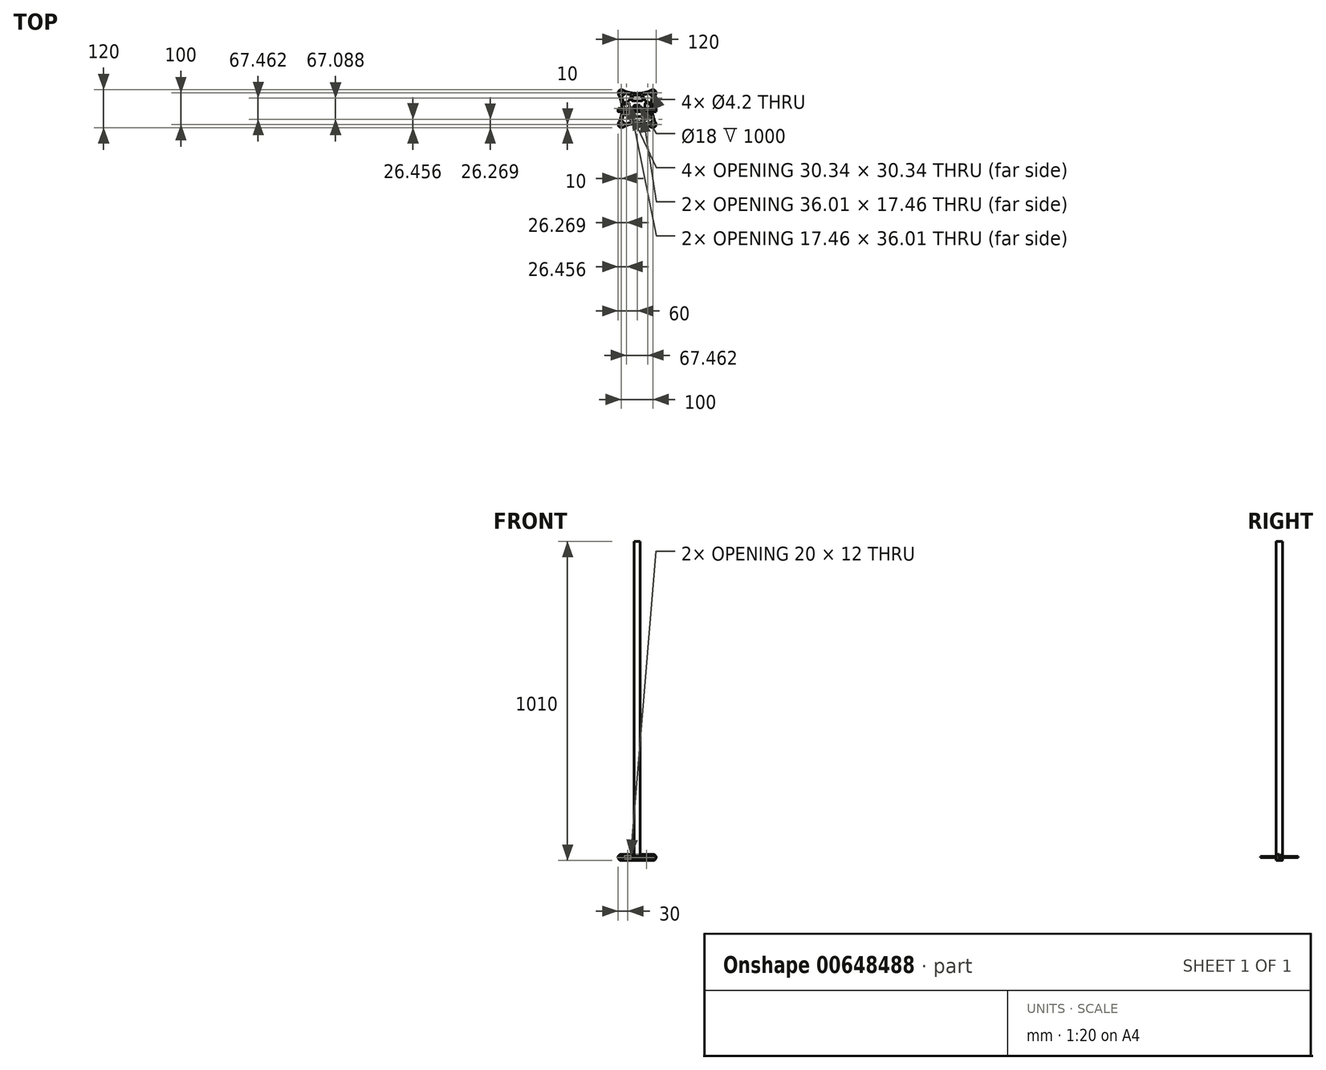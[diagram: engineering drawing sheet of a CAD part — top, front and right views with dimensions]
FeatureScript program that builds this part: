
annotation { "Feature Type Name" : "Feature", "Feature Type Description" : "" }
export const myFeature = defineFeature(function(context is Context, id is Id, definition is map)
    precondition{}
    {
        {
            var Q0;
            Q0=qCreatedBy(makeId("Top.planeOp"),FACE);
            var sketch = newSketch(context, id + "F0", { "sketchPlane" : qUnion([Q0])});
            skCircle(sketch, "E0", {"center": v(0, 0) * mm, "radius": 10 * mm});
            skCircle(sketch, "E1", {"center": v(0, 0) * mm, "radius": 9 * mm});
            skSolve(sketch);
        }
        {
            var Q0;
            Q0=makeQuery(id+"F0.imprint","IMPRINT",FACE,{"disambiguationData":[TD([[makeQuery(id+"F0.imprint","IMPRINT",EDGE,{"derivedFrom":sQuery(id+"F0.wireOp",EDGE,"335d696f-6c34-485e-b587-ec5af4deedc00.MirrorC")}),1.0]])]});
            var Q1;
            Q1=makeQuery(id+"F0.imprint","IMPRINT",FACE,{"disambiguationData":[TD([[makeQuery(id+"F0.imprint","IMPRINT",EDGE,{"derivedFrom":sQuery(id+"F0.wireOp",EDGE,"E0")}),1.0]])]});
            extrude(context, id + "F1", {"entities" : qUnion([Q0, Q1]), "depth" : 1000 * mm, "offsetDistance" : 25 * mm});
        }
        {
            var Q0;
            Q0=qCreatedBy(makeId("Top.planeOp"),FACE);
            var sketch = newSketch(context, id + "F2", { "sketchPlane" : qUnion([Q0])});
            skLineSegment(sketch, "E2", {"start": v(0, 0) * mm, "end": v(9, 0) * mm});
            skLineSegment(sketch, "E3", {"start": v(9, 0) * mm, "end": v(9, 7) * mm});
            skLineSegment(sketch, "E4", {"start": v(9, 7) * mm, "end": v(10, 7) * mm});
            skLineSegment(sketch, "E5", {"start": v(10, 7) * mm, "end": v(10, 10) * mm});
            skLineSegment(sketch, "E6", {"start": v(10, 10) * mm, "end": v(2.5, 10) * mm});
            skLineSegment(sketch, "E7", {"start": v(2.5, 10) * mm, "end": v(2.5, 4) * mm});
            skLineSegment(sketch, "E8", {"start": v(2.5, 4) * mm, "end": v(0, 4) * mm});
            skLineSegment(sketch, "E9", {"start": v(0, 4) * mm, "end": v(0, 0) * mm});
            skLineSegment(sketch, "E10", {"start": v(0, 20) * mm, "end": v(0, -14.34) * mm, "construction": true});
            skSolve(sketch);
        }
        {
            var Q0;
            Q0=makeQuery(id+"F2.imprint","IMPRINT",FACE,{"disambiguationData":[TD([[makeQuery(id+"F2.imprint","IMPRINT",EDGE,{"derivedFrom":sQuery(id+"F2.wireOp",EDGE,"E2")}),1.0]])]});
            var Q1;
            Q1=sQuery(id+"F2.wireOp",EDGE,"E10");
            revolve(context, id + "F3", {"surfaceOperationType" : NewSurfaceOperationType.NEW, "entities" : qUnion([Q0]), "axis" : qUnion([Q1]), "revolveType" : RevolveType.FULL});
        }
        {
            var Q0;
            Q0=qCreatedBy(makeId("Front.planeOp"),FACE);
            var sketch = newSketch(context, id + "F4", { "sketchPlane" : qUnion([Q0])});
            skCircle(sketch, "E11", {"center": v(50, 0) * mm, "radius": 3.1 * mm});
            skArc(sketch, "E12", {"start": v(50, -10) * mm, "mid": v(60, 0) * mm, "end": v(50, 10) * mm});
            skLineSegment(sketch, "E13.bottom", {"start": v(40, 6) * mm, "end": v(20, 6) * mm});
            skLineSegment(sketch, "E13.top", {"start": v(40, -6) * mm, "end": v(20, -6) * mm});
            skLineSegment(sketch, "E13.left", {"start": v(40, 6) * mm, "end": v(40, -6) * mm});
            skLineSegment(sketch, "E13.right", {"start": v(20, 6) * mm, "end": v(20, -6) * mm});
            skPoint(sketch, "E13.middle", {"position": v(30, 0) * mm});
            skLineSegment(sketch, "E14.MirrorCS", {"start": v(-20, 6) * mm, "end": v(-20, -6) * mm});
            skLineSegment(sketch, "E15.MirrorCS", {"start": v(-40, 6) * mm, "end": v(-20, 6) * mm});
            skLineSegment(sketch, "E16.MirrorCS", {"start": v(-40, -6) * mm, "end": v(-20, -6) * mm});
            skLineSegment(sketch, "E17.MirrorCS", {"start": v(-40, 6) * mm, "end": v(-40, -6) * mm});
            skArc(sketch, "E18.MirrorCS", {"start": v(-50, -10) * mm, "mid": v(-60, 0) * mm, "end": v(-50, 10) * mm});
            skCircle(sketch, "E19.MirrorC", {"center": v(-50, 0) * mm, "radius": 3.1 * mm});
            skLineSegment(sketch, "E20", {"start": v(50, 10) * mm, "end": v(15, 10) * mm});
            skLineSegment(sketch, "E21", {"start": v(15, 10) * mm, "end": v(15, 6.3) * mm});
            skLineSegment(sketch, "E22", {"start": v(15, 6.3) * mm, "end": v(5.1, 6.3) * mm});
            skLineSegment(sketch, "E23", {"start": v(5.1, 6.3) * mm, "end": v(5.1, -6) * mm});
            skLineSegment(sketch, "E24", {"start": v(5.1, -6) * mm, "end": v(0, -6) * mm});
            skLineSegment(sketch, "E25.MirrorCS", {"start": v(-5.1, -6) * mm, "end": v(0, -6) * mm});
            skLineSegment(sketch, "E26.MirrorCS", {"start": v(-5.1, 6.3) * mm, "end": v(-5.1, -6) * mm});
            skLineSegment(sketch, "E27.MirrorCS", {"start": v(-15, 6.3) * mm, "end": v(-5.1, 6.3) * mm});
            skLineSegment(sketch, "E28.MirrorCS", {"start": v(-15, 10) * mm, "end": v(-15, 6.3) * mm});
            skLineSegment(sketch, "E29.MirrorCS", {"start": v(-50, 10) * mm, "end": v(-15, 10) * mm});
            skLineSegment(sketch, "E30", {"start": v(50, -10) * mm, "end": v(0, -10) * mm});
            skLineSegment(sketch, "E31.MirrorCS", {"start": v(-50, -10) * mm, "end": v(0, -10) * mm});
            skSolve(sketch);
        }
        {
            var Q0;
            Q0=makeQuery(id+"F4.imprint","IMPRINT",FACE,{"disambiguationData":[TD([[makeQuery(id+"F4.imprint","IMPRINT",EDGE,{"derivedFrom":sQuery(id+"F4.wireOp",EDGE,"E11")}),-1.0]])]});
            extrude(context, id + "F5", {"entities" : qUnion([Q0]), "depth" : 10 * mm, "offsetDistance" : 25 * mm});
        }
        {
            var Q0;
            Q0=makeQuery(id+"F5.opExtrude","SWEPT_EDGE",EDGE,{"disambiguationData":[OSD([sQuery(id+"F4.wireOp",EDGE,"E15.MirrorCS"),sQuery(id+"F4.wireOp",EDGE,"E17.MirrorCS")])]});
            var Q1;
            Q1=makeQuery(id+"F5.opExtrude","SWEPT_EDGE",EDGE,{"disambiguationData":[OSD([sQuery(id+"F4.wireOp",EDGE,"E14.MirrorCS"),sQuery(id+"F4.wireOp",EDGE,"E15.MirrorCS")])]});
            var Q2;
            Q2=makeQuery(id+"F5.opExtrude","SWEPT_EDGE",EDGE,{"disambiguationData":[OSD([sQuery(id+"F4.wireOp",EDGE,"E14.MirrorCS"),sQuery(id+"F4.wireOp",EDGE,"E16.MirrorCS")])]});
            var Q3;
            Q3=makeQuery(id+"F5.opExtrude","SWEPT_EDGE",EDGE,{"disambiguationData":[OSD([sQuery(id+"F4.wireOp",EDGE,"E13.top"),sQuery(id+"F4.wireOp",EDGE,"E13.left")])]});
            var Q4;
            Q4=makeQuery(id+"F5.opExtrude","SWEPT_EDGE",EDGE,{"disambiguationData":[OSD([sQuery(id+"F4.wireOp",EDGE,"E16.MirrorCS"),sQuery(id+"F4.wireOp",EDGE,"E17.MirrorCS")])]});
            var Q5;
            Q5=makeQuery(id+"F5.opExtrude","SWEPT_EDGE",EDGE,{"disambiguationData":[OSD([sQuery(id+"F4.wireOp",EDGE,"E13.top"),sQuery(id+"F4.wireOp",EDGE,"E13.right")])]});
            var Q6;
            Q6=makeQuery(id+"F5.opExtrude","SWEPT_EDGE",EDGE,{"disambiguationData":[OSD([sQuery(id+"F4.wireOp",EDGE,"E13.bottom"),sQuery(id+"F4.wireOp",EDGE,"E13.left")])]});
            var Q7;
            Q7=makeQuery(id+"F5.opExtrude","SWEPT_EDGE",EDGE,{"disambiguationData":[OSD([sQuery(id+"F4.wireOp",EDGE,"E13.bottom"),sQuery(id+"F4.wireOp",EDGE,"E13.right")])]});
            var Q8;
            Q8=makeQuery(id+"F5.opExtrude","SWEPT_EDGE",EDGE,{"disambiguationData":[OSD([sQuery(id+"F4.wireOp",EDGE,"E25.MirrorCS"),sQuery(id+"F4.wireOp",EDGE,"E26.MirrorCS")])]});
            var Q9;
            Q9=makeQuery(id+"F5.opExtrude","SWEPT_EDGE",EDGE,{"disambiguationData":[OSD([sQuery(id+"F4.wireOp",EDGE,"E23"),sQuery(id+"F4.wireOp",EDGE,"E24")])]});
            fillet(context, id + "F6", {"entities" : qUnion([Q0, Q1, Q2, Q3, Q4, Q5, Q6, Q7, Q8, Q9]), "radius" : 3 * mm, "tangentPropagation" : true, "allowEdgeOverflow" : false});
        }
        {
            var Q0;
            Q0=qCreatedBy(makeId("Top.planeOp"),FACE);
            var sketch = newSketch(context, id + "F7", { "sketchPlane" : qUnion([Q0])});
            skLineSegment(sketch, "E32.bottom", {"start": v(50, 50) * mm, "end": v(-50, 50) * mm, "construction": true});
            skLineSegment(sketch, "E32.top", {"start": v(50, -50) * mm, "end": v(-50, -50) * mm, "construction": true});
            skLineSegment(sketch, "E32.left", {"start": v(50, 50) * mm, "end": v(50, -50) * mm, "construction": true});
            skLineSegment(sketch, "E32.right", {"start": v(-50, 50) * mm, "end": v(-50, -50) * mm, "construction": true});
            skPoint(sketch, "E32.middle", {"position": v(0, 0) * mm});
            skArc(sketch, "E33", {"start": v(0, 48) * mm, "mid": v(23.12, 50.7) * mm, "end": v(45, 58.66) * mm});
            skArc(sketch, "E34", {"start": v(45, 58.66) * mm, "mid": v(57.07, 57.07) * mm, "end": v(58.66, 45) * mm});
            skArc(sketch, "E35", {"start": v(58.66, 45) * mm, "mid": v(50.7, 23.12) * mm, "end": v(48, 0) * mm});
            skLineSegment(sketch, "E36", {"start": v(50, 50) * mm, "end": v(45, 58.66) * mm, "construction": true});
            skLineSegment(sketch, "E37", {"start": v(50, 50) * mm, "end": v(58.66, 45) * mm, "construction": true});
            skCircle(sketch, "E38", {"center": v(50, 50) * mm, "radius": 2.1 * mm});
            skArc(sketch, "E39.MirrorCS", {"start": v(0, 48) * mm, "mid": v(-23.12, 50.7) * mm, "end": v(-45, 58.66) * mm});
            skArc(sketch, "E40.MirrorCS", {"start": v(-45, 58.66) * mm, "mid": v(-57.07, 57.07) * mm, "end": v(-58.66, 45) * mm});
            skCircle(sketch, "E41.MirrorC", {"center": v(-50, 50) * mm, "radius": 2.1 * mm});
            skArc(sketch, "E42.MirrorCS", {"start": v(-58.66, 45) * mm, "mid": v(-50.7, 23.12) * mm, "end": v(-48, 0) * mm});
            skArc(sketch, "E43.MirrorCS", {"start": v(-58.66, -45) * mm, "mid": v(-50.7, -23.12) * mm, "end": v(-48, 0) * mm});
            skArc(sketch, "E44.MirrorCS", {"start": v(-45, -58.66) * mm, "mid": v(-57.07, -57.07) * mm, "end": v(-58.66, -45) * mm});
            skCircle(sketch, "E45.MirrorC", {"center": v(-50, -50) * mm, "radius": 2.1 * mm});
            skArc(sketch, "E46.MirrorCS", {"start": v(0, -48) * mm, "mid": v(-23.12, -50.7) * mm, "end": v(-45, -58.66) * mm});
            skArc(sketch, "E47.MirrorCS", {"start": v(0, -48) * mm, "mid": v(23.12, -50.7) * mm, "end": v(45, -58.66) * mm});
            skArc(sketch, "E48.MirrorCS", {"start": v(45, -58.66) * mm, "mid": v(57.07, -57.07) * mm, "end": v(58.66, -45) * mm});
            skArc(sketch, "E49.MirrorCS", {"start": v(58.66, -45) * mm, "mid": v(50.7, -23.12) * mm, "end": v(48, 0) * mm});
            skCircle(sketch, "E50.MirrorC", {"center": v(50, -50) * mm, "radius": 2.1 * mm});
            skArc(sketch, "E51", {"start": v(40, 49.81) * mm, "mid": v(42.93, 42.93) * mm, "end": v(49.81, 40) * mm});
            skArc(sketch, "E52", {"start": v(0, 42) * mm, "mid": v(6, 42.17) * mm, "end": v(12, 42.68) * mm});
            skArc(sketch, "E53", {"start": v(40, 49.81) * mm, "mid": v(28.75, 45.96) * mm, "end": v(17.13, 43.39) * mm});
            skLineSegment(sketch, "E54", {"start": v(0, 25) * mm, "end": v(19.56, 25) * mm});
            skLineSegment(sketch, "E55", {"start": v(19.56, 25) * mm, "end": v(12, 42.68) * mm});
            skLineSegment(sketch, "E56", {"start": v(25, 25) * mm, "end": v(17.13, 43.39) * mm});
            skArc(sketch, "E57", {"start": v(49.81, 40) * mm, "mid": v(45.96, 28.75) * mm, "end": v(43.39, 17.13) * mm});
            skArc(sketch, "E58", {"start": v(42.68, 12) * mm, "mid": v(42.17, 6) * mm, "end": v(42, 0) * mm});
            skLineSegment(sketch, "E59", {"start": v(25, 25) * mm, "end": v(43.39, 17.13) * mm});
            skLineSegment(sketch, "E60", {"start": v(42.68, 12) * mm, "end": v(25, 19.56) * mm});
            skLineSegment(sketch, "E61", {"start": v(25, 19.56) * mm, "end": v(25, 0) * mm});
            skLineSegment(sketch, "E62.MirrorCS", {"start": v(0, 25) * mm, "end": v(-19.56, 25) * mm});
            skArc(sketch, "E63.MirrorCS", {"start": v(0, 42) * mm, "mid": v(-6, 42.17) * mm, "end": v(-12, 42.68) * mm});
            skArc(sketch, "E64.MirrorCS", {"start": v(-40, 49.81) * mm, "mid": v(-28.75, 45.96) * mm, "end": v(-17.13, 43.39) * mm});
            skArc(sketch, "E65.MirrorCS", {"start": v(-40, 49.81) * mm, "mid": v(-42.93, 42.93) * mm, "end": v(-49.81, 40) * mm});
            skArc(sketch, "E66.MirrorCS", {"start": v(-49.81, 40) * mm, "mid": v(-45.96, 28.75) * mm, "end": v(-43.39, 17.13) * mm});
            skLineSegment(sketch, "E67.MirrorCS", {"start": v(-25, 25) * mm, "end": v(-43.39, 17.13) * mm});
            skLineSegment(sketch, "E68.MirrorCS", {"start": v(-19.56, 25) * mm, "end": v(-12, 42.68) * mm});
            skLineSegment(sketch, "E69.MirrorCS", {"start": v(-25, 25) * mm, "end": v(-17.13, 43.39) * mm});
            skLineSegment(sketch, "E70.MirrorCS", {"start": v(-42.68, 12) * mm, "end": v(-25, 19.56) * mm});
            skLineSegment(sketch, "E71.MirrorCS", {"start": v(-25, 19.56) * mm, "end": v(-25, 0) * mm});
            skArc(sketch, "E72.MirrorCS", {"start": v(-42.68, 12) * mm, "mid": v(-42.17, 6) * mm, "end": v(-42, 0) * mm});
            skArc(sketch, "E73.MirrorCS", {"start": v(-42.68, -12) * mm, "mid": v(-42.17, -6) * mm, "end": v(-42, 0) * mm});
            skLineSegment(sketch, "E74.MirrorCS", {"start": v(-42.68, -12) * mm, "end": v(-25, -19.56) * mm});
            skLineSegment(sketch, "E75.MirrorCS", {"start": v(-25, -19.56) * mm, "end": v(-25, 0) * mm});
            skLineSegment(sketch, "E76.MirrorCS", {"start": v(-25, -25) * mm, "end": v(-17.13, -43.39) * mm});
            skLineSegment(sketch, "E77.MirrorCS", {"start": v(-25, -25) * mm, "end": v(-43.39, -17.13) * mm});
            skArc(sketch, "E78.MirrorCS", {"start": v(-49.81, -40) * mm, "mid": v(-45.96, -28.75) * mm, "end": v(-43.39, -17.13) * mm});
            skArc(sketch, "E79.MirrorCS", {"start": v(-40, -49.81) * mm, "mid": v(-42.93, -42.93) * mm, "end": v(-49.81, -40) * mm});
            skArc(sketch, "E80.MirrorCS", {"start": v(-40, -49.81) * mm, "mid": v(-28.75, -45.96) * mm, "end": v(-17.13, -43.39) * mm});
            skArc(sketch, "E81.MirrorCS", {"start": v(0, -42) * mm, "mid": v(-6, -42.17) * mm, "end": v(-12, -42.68) * mm});
            skLineSegment(sketch, "E82.MirrorCS", {"start": v(0, -25) * mm, "end": v(-19.56, -25) * mm});
            skLineSegment(sketch, "E83.MirrorCS", {"start": v(0, -25) * mm, "end": v(19.56, -25) * mm});
            skLineSegment(sketch, "E84.MirrorCS", {"start": v(19.56, -25) * mm, "end": v(12, -42.68) * mm});
            skLineSegment(sketch, "E85.MirrorCS", {"start": v(-19.56, -25) * mm, "end": v(-12, -42.68) * mm});
            skArc(sketch, "E86.MirrorCS", {"start": v(0, -42) * mm, "mid": v(6, -42.17) * mm, "end": v(12, -42.68) * mm});
            skArc(sketch, "E87.MirrorCS", {"start": v(40, -49.81) * mm, "mid": v(28.75, -45.96) * mm, "end": v(17.13, -43.39) * mm});
            skLineSegment(sketch, "E88.MirrorCS", {"start": v(25, -25) * mm, "end": v(17.13, -43.39) * mm});
            skLineSegment(sketch, "E89.MirrorCS", {"start": v(25, -25) * mm, "end": v(43.39, -17.13) * mm});
            skArc(sketch, "E90.MirrorCS", {"start": v(49.81, -40) * mm, "mid": v(45.96, -28.75) * mm, "end": v(43.39, -17.13) * mm});
            skArc(sketch, "E91.MirrorCS", {"start": v(40, -49.81) * mm, "mid": v(42.93, -42.93) * mm, "end": v(49.81, -40) * mm});
            skLineSegment(sketch, "E92.MirrorCS", {"start": v(25, -19.56) * mm, "end": v(25, 0) * mm});
            skLineSegment(sketch, "E93.MirrorCS", {"start": v(42.68, -12) * mm, "end": v(25, -19.56) * mm});
            skArc(sketch, "E94.MirrorCS", {"start": v(42.68, -12) * mm, "mid": v(42.17, -6) * mm, "end": v(42, 0) * mm});
            skSolve(sketch);
        }
        {
            var Q0;
            Q0=makeQuery(id+"F7.imprint","IMPRINT",FACE,{"disambiguationData":[TD([[makeQuery(id+"F7.imprint","IMPRINT",EDGE,{"derivedFrom":sQuery(id+"F7.wireOp",EDGE,"E33")}),-1.0]])]});
            extrude(context, id + "F8", {"entities" : qUnion([Q0]), "depth" : 3.7 * mm, "offsetDistance" : 25 * mm});
        }
        {
            var Q0;
            Q0=makeQuery(id+"F8.opExtrude","SWEPT_EDGE",EDGE,{"disambiguationData":[OSD([sQuery(id+"F7.wireOp",EDGE,"E64.MirrorCS"),sQuery(id+"F7.wireOp",EDGE,"E65.MirrorCS")])]});
            var Q1;
            Q1=makeQuery(id+"F8.opExtrude","SWEPT_EDGE",EDGE,{"disambiguationData":[OSD([sQuery(id+"F7.wireOp",EDGE,"E65.MirrorCS"),sQuery(id+"F7.wireOp",EDGE,"E66.MirrorCS")])]});
            var Q2;
            Q2=makeQuery(id+"F8.opExtrude","SWEPT_EDGE",EDGE,{"disambiguationData":[OSD([sQuery(id+"F7.wireOp",EDGE,"E64.MirrorCS"),sQuery(id+"F7.wireOp",EDGE,"E69.MirrorCS")])]});
            var Q3;
            Q3=makeQuery(id+"F8.opExtrude","SWEPT_EDGE",EDGE,{"disambiguationData":[OSD([sQuery(id+"F7.wireOp",EDGE,"E67.MirrorCS"),sQuery(id+"F7.wireOp",EDGE,"E69.MirrorCS")])]});
            var Q4;
            Q4=makeQuery(id+"F8.opExtrude","SWEPT_EDGE",EDGE,{"disambiguationData":[OSD([sQuery(id+"F7.wireOp",EDGE,"E66.MirrorCS"),sQuery(id+"F7.wireOp",EDGE,"E67.MirrorCS")])]});
            var Q5;
            Q5=makeQuery(id+"F8.opExtrude","SWEPT_EDGE",EDGE,{"disambiguationData":[OSD([sQuery(id+"F7.wireOp",EDGE,"E73.MirrorCS"),sQuery(id+"F7.wireOp",EDGE,"E74.MirrorCS")])]});
            var Q6;
            Q6=makeQuery(id+"F8.opExtrude","SWEPT_EDGE",EDGE,{"disambiguationData":[OSD([sQuery(id+"F7.wireOp",EDGE,"E78.MirrorCS"),sQuery(id+"F7.wireOp",EDGE,"E79.MirrorCS")])]});
            var Q7;
            Q7=makeQuery(id+"F8.opExtrude","SWEPT_EDGE",EDGE,{"disambiguationData":[OSD([sQuery(id+"F7.wireOp",EDGE,"E79.MirrorCS"),sQuery(id+"F7.wireOp",EDGE,"E80.MirrorCS")])]});
            var Q8;
            Q8=makeQuery(id+"F8.opExtrude","SWEPT_EDGE",EDGE,{"disambiguationData":[OSD([sQuery(id+"F7.wireOp",EDGE,"E70.MirrorCS"),sQuery(id+"F7.wireOp",EDGE,"E72.MirrorCS")])]});
            var Q9;
            Q9=makeQuery(id+"F8.opExtrude","SWEPT_EDGE",EDGE,{"disambiguationData":[OSD([sQuery(id+"F7.wireOp",EDGE,"E76.MirrorCS"),sQuery(id+"F7.wireOp",EDGE,"E77.MirrorCS")])]});
            var Q10;
            Q10=makeQuery(id+"F8.opExtrude","SWEPT_EDGE",EDGE,{"disambiguationData":[OSD([sQuery(id+"F7.wireOp",EDGE,"E63.MirrorCS"),sQuery(id+"F7.wireOp",EDGE,"E68.MirrorCS")])]});
            var Q11;
            Q11=makeQuery(id+"F8.opExtrude","SWEPT_EDGE",EDGE,{"disambiguationData":[OSD([sQuery(id+"F7.wireOp",EDGE,"E52"),sQuery(id+"F7.wireOp",EDGE,"E55")])]});
            var Q12;
            Q12=makeQuery(id+"F8.opExtrude","SWEPT_EDGE",EDGE,{"disambiguationData":[OSD([sQuery(id+"F7.wireOp",EDGE,"E70.MirrorCS"),sQuery(id+"F7.wireOp",EDGE,"E71.MirrorCS")])]});
            var Q13;
            Q13=makeQuery(id+"F8.opExtrude","SWEPT_EDGE",EDGE,{"disambiguationData":[OSD([sQuery(id+"F7.wireOp",EDGE,"E54"),sQuery(id+"F7.wireOp",EDGE,"E55")])]});
            var Q14;
            Q14=makeQuery(id+"F8.opExtrude","SWEPT_EDGE",EDGE,{"disambiguationData":[OSD([sQuery(id+"F7.wireOp",EDGE,"E57"),sQuery(id+"F7.wireOp",EDGE,"E59")])]});
            var Q15;
            Q15=makeQuery(id+"F8.opExtrude","SWEPT_EDGE",EDGE,{"disambiguationData":[OSD([sQuery(id+"F7.wireOp",EDGE,"E93.MirrorCS"),sQuery(id+"F7.wireOp",EDGE,"E94.MirrorCS")])]});
            var Q16;
            Q16=makeQuery(id+"F8.opExtrude","SWEPT_EDGE",EDGE,{"disambiguationData":[OSD([sQuery(id+"F7.wireOp",EDGE,"E90.MirrorCS"),sQuery(id+"F7.wireOp",EDGE,"E91.MirrorCS")])]});
            var Q17;
            Q17=makeQuery(id+"F8.opExtrude","SWEPT_EDGE",EDGE,{"disambiguationData":[OSD([sQuery(id+"F7.wireOp",EDGE,"E84.MirrorCS"),sQuery(id+"F7.wireOp",EDGE,"E86.MirrorCS")])]});
            var Q18;
            Q18=makeQuery(id+"F8.opExtrude","SWEPT_EDGE",EDGE,{"disambiguationData":[OSD([sQuery(id+"F7.wireOp",EDGE,"E76.MirrorCS"),sQuery(id+"F7.wireOp",EDGE,"E80.MirrorCS")])]});
            var Q19;
            Q19=makeQuery(id+"F8.opExtrude","SWEPT_EDGE",EDGE,{"disambiguationData":[OSD([sQuery(id+"F7.wireOp",EDGE,"E74.MirrorCS"),sQuery(id+"F7.wireOp",EDGE,"E75.MirrorCS")])]});
            var Q20;
            Q20=makeQuery(id+"F8.opExtrude","SWEPT_EDGE",EDGE,{"disambiguationData":[OSD([sQuery(id+"F7.wireOp",EDGE,"E87.MirrorCS"),sQuery(id+"F7.wireOp",EDGE,"E91.MirrorCS")])]});
            var Q21;
            Q21=makeQuery(id+"F8.opExtrude","SWEPT_EDGE",EDGE,{"disambiguationData":[OSD([sQuery(id+"F7.wireOp",EDGE,"E58"),sQuery(id+"F7.wireOp",EDGE,"E60")])]});
            var Q22;
            Q22=makeQuery(id+"F8.opExtrude","SWEPT_EDGE",EDGE,{"disambiguationData":[OSD([sQuery(id+"F7.wireOp",EDGE,"E83.MirrorCS"),sQuery(id+"F7.wireOp",EDGE,"E84.MirrorCS")])]});
            var Q23;
            Q23=makeQuery(id+"F8.opExtrude","SWEPT_EDGE",EDGE,{"disambiguationData":[OSD([sQuery(id+"F7.wireOp",EDGE,"E89.MirrorCS"),sQuery(id+"F7.wireOp",EDGE,"E90.MirrorCS")])]});
            var Q24;
            Q24=makeQuery(id+"F8.opExtrude","SWEPT_EDGE",EDGE,{"disambiguationData":[OSD([sQuery(id+"F7.wireOp",EDGE,"E51"),sQuery(id+"F7.wireOp",EDGE,"E57")])]});
            var Q25;
            Q25=makeQuery(id+"F8.opExtrude","SWEPT_EDGE",EDGE,{"disambiguationData":[OSD([sQuery(id+"F7.wireOp",EDGE,"E51"),sQuery(id+"F7.wireOp",EDGE,"E53")])]});
            var Q26;
            Q26=makeQuery(id+"F8.opExtrude","SWEPT_EDGE",EDGE,{"disambiguationData":[OSD([sQuery(id+"F7.wireOp",EDGE,"E60"),sQuery(id+"F7.wireOp",EDGE,"E61")])]});
            var Q27;
            Q27=makeQuery(id+"F8.opExtrude","SWEPT_EDGE",EDGE,{"disambiguationData":[OSD([sQuery(id+"F7.wireOp",EDGE,"E53"),sQuery(id+"F7.wireOp",EDGE,"E56")])]});
            var Q28;
            Q28=makeQuery(id+"F8.opExtrude","SWEPT_EDGE",EDGE,{"disambiguationData":[OSD([sQuery(id+"F7.wireOp",EDGE,"E82.MirrorCS"),sQuery(id+"F7.wireOp",EDGE,"E85.MirrorCS")])]});
            var Q29;
            Q29=makeQuery(id+"F8.opExtrude","SWEPT_EDGE",EDGE,{"disambiguationData":[OSD([sQuery(id+"F7.wireOp",EDGE,"E88.MirrorCS"),sQuery(id+"F7.wireOp",EDGE,"E89.MirrorCS")])]});
            var Q30;
            Q30=makeQuery(id+"F8.opExtrude","SWEPT_EDGE",EDGE,{"disambiguationData":[OSD([sQuery(id+"F7.wireOp",EDGE,"E81.MirrorCS"),sQuery(id+"F7.wireOp",EDGE,"E85.MirrorCS")])]});
            var Q31;
            Q31=makeQuery(id+"F8.opExtrude","SWEPT_EDGE",EDGE,{"disambiguationData":[OSD([sQuery(id+"F7.wireOp",EDGE,"E87.MirrorCS"),sQuery(id+"F7.wireOp",EDGE,"E88.MirrorCS")])]});
            var Q32;
            Q32=makeQuery(id+"F8.opExtrude","SWEPT_EDGE",EDGE,{"disambiguationData":[OSD([sQuery(id+"F7.wireOp",EDGE,"E56"),sQuery(id+"F7.wireOp",EDGE,"E59")])]});
            var Q33;
            Q33=makeQuery(id+"F8.opExtrude","SWEPT_EDGE",EDGE,{"disambiguationData":[OSD([sQuery(id+"F7.wireOp",EDGE,"E62.MirrorCS"),sQuery(id+"F7.wireOp",EDGE,"E68.MirrorCS")])]});
            var Q34;
            Q34=makeQuery(id+"F8.opExtrude","SWEPT_EDGE",EDGE,{"disambiguationData":[OSD([sQuery(id+"F7.wireOp",EDGE,"E92.MirrorCS"),sQuery(id+"F7.wireOp",EDGE,"E93.MirrorCS")])]});
            var Q35;
            Q35=makeQuery(id+"F8.opExtrude","SWEPT_EDGE",EDGE,{"disambiguationData":[OSD([sQuery(id+"F7.wireOp",EDGE,"E77.MirrorCS"),sQuery(id+"F7.wireOp",EDGE,"E78.MirrorCS")])]});
            fillet(context, id + "F9", {"entities" : qUnion([Q0, Q1, Q2, Q3, Q4, Q5, Q6, Q7, Q8, Q9, Q10, Q11, Q12, Q13, Q14, Q15, Q16, Q17, Q18, Q19, Q20, Q21, Q22, Q23, Q24, Q25, Q26, Q27, Q28, Q29, Q30, Q31, Q32, Q33, Q34, Q35]), "radius" : 3 * mm, "tangentPropagation" : true, "allowEdgeOverflow" : false});
        }
        {
            var Q0;
            Q0=qCreatedBy(makeId("Top.planeOp"),FACE);
            var sketch = newSketch(context, id + "F10", { "sketchPlane" : qUnion([Q0])});
            skLineSegment(sketch, "E95.bottom", {"start": v(14.9, 5) * mm, "end": v(-14.9, 5) * mm});
            skLineSegment(sketch, "E95.top", {"start": v(14.9, -5) * mm, "end": v(-14.9, -5) * mm});
            skLineSegment(sketch, "E95.left", {"start": v(14.9, 5) * mm, "end": v(14.9, -5) * mm});
            skLineSegment(sketch, "E95.right", {"start": v(-14.9, 5) * mm, "end": v(-14.9, -5) * mm});
            skPoint(sketch, "E95.middle", {"position": v(0, 0) * mm});
            skCircle(sketch, "E96", {"center": v(10, 0) * mm, "radius": 1.6 * mm});
            skCircle(sketch, "E97.MirrorC", {"center": v(-10, 0) * mm, "radius": 1.6 * mm});
            skSolve(sketch);
        }
        {
            var Q0;
            Q0=makeQuery(id+"F10.imprint","IMPRINT",FACE,{"disambiguationData":[TD([[makeQuery(id+"F10.imprint","IMPRINT",EDGE,{"derivedFrom":sQuery(id+"F10.wireOp",EDGE,"E95.bottom")}),1.0]])]});
            extrude(context, id + "F11", {"entities" : qUnion([Q0]), "depth" : 3.7 * mm, "offsetDistance" : 25 * mm});
        }
        {
            var Q0;
            Q0=makeQuery(id+"F5.opExtrude","SWEPT_FACE",FACE,{"disambiguationData":[OSD([sQuery(id+"F4.wireOp",EDGE,"E27.MirrorCS")])]});
            var sketch = newSketch(context, id + "F12", { "sketchPlane" : qUnion([Q0])});
            skPoint(sketch, "E98", {"position": v(-10.05, -5) * mm});
            skPoint(sketch, "E98.positionSnap0", {"position": v(-10.05, 0) * mm});
            skPoint(sketch, "E98.positionSnap1", {"position": v(-5.1, -5) * mm});
            skPoint(sketch, "E99", {"position": v(10.1, -5) * mm});
            skSolve(sketch);
        }
        {
            var Q0;
            Q0=sQuery(id+"F12.wireOp",VERTEX,"E98");
            var Q1;
            Q1=sQuery(id+"F12.wireOp",VERTEX,"E99");
            var Q2;
            Q2=makeQuery(id+"F5.opExtrude","SWEPT_BODY",BODY,{"disambiguationData":[OSD([sQuery(id+"F4.wireOp",EDGE,"E11"),sQuery(id+"F4.wireOp",EDGE,"E12"),sQuery(id+"F4.wireOp",EDGE,"E13.bottom"),sQuery(id+"F4.wireOp",EDGE,"E13.top"),sQuery(id+"F4.wireOp",EDGE,"E13.left"),sQuery(id+"F4.wireOp",EDGE,"E13.right"),sQuery(id+"F4.wireOp",EDGE,"E14.MirrorCS"),sQuery(id+"F4.wireOp",EDGE,"E15.MirrorCS"),sQuery(id+"F4.wireOp",EDGE,"E16.MirrorCS"),sQuery(id+"F4.wireOp",EDGE,"E17.MirrorCS"),sQuery(id+"F4.wireOp",EDGE,"E18.MirrorCS"),sQuery(id+"F4.wireOp",EDGE,"E19.MirrorC"),sQuery(id+"F4.wireOp",EDGE,"E20"),sQuery(id+"F4.wireOp",EDGE,"E21"),sQuery(id+"F4.wireOp",EDGE,"E22"),sQuery(id+"F4.wireOp",EDGE,"E23"),sQuery(id+"F4.wireOp",EDGE,"E24"),sQuery(id+"F4.wireOp",EDGE,"E25.MirrorCS"),sQuery(id+"F4.wireOp",EDGE,"E26.MirrorCS"),sQuery(id+"F4.wireOp",EDGE,"E27.MirrorCS"),sQuery(id+"F4.wireOp",EDGE,"E28.MirrorCS"),sQuery(id+"F4.wireOp",EDGE,"E29.MirrorCS"),sQuery(id+"F4.wireOp",EDGE,"E30"),sQuery(id+"F4.wireOp",EDGE,"E31.MirrorCS")])]});
            hole(context, id + "F13", {"style" : HoleStyle.SIMPLE, "endStyle" : HoleEndStyle.BLIND, "standardTappedOrClearance" : lookupTablePath({ "standard" : "ISO", "engagement" : "75%", "pitch" : "0.5 mm", "size" : "M3", "type" : "Tapped" }), "standardBlindInLast" : lookupTablePath({ "standard" : "ISO", "engagement" : "75%", "pitch" : "0.5 mm", "size" : "M3", "type" : "Tapped" }), "holeDiameter" : 2.5 * mm, "majorDiameter" : 3 * mm, "showTappedDepth" : true, "holeDepth" : 8 * mm, "isTappedThrough" : true, "tappedDepth" : 6.5 * mm, "tapClearance" : 3, "locations" : qUnion([Q0, Q1]), "scope" : qUnion([Q2])});
        }
    });
